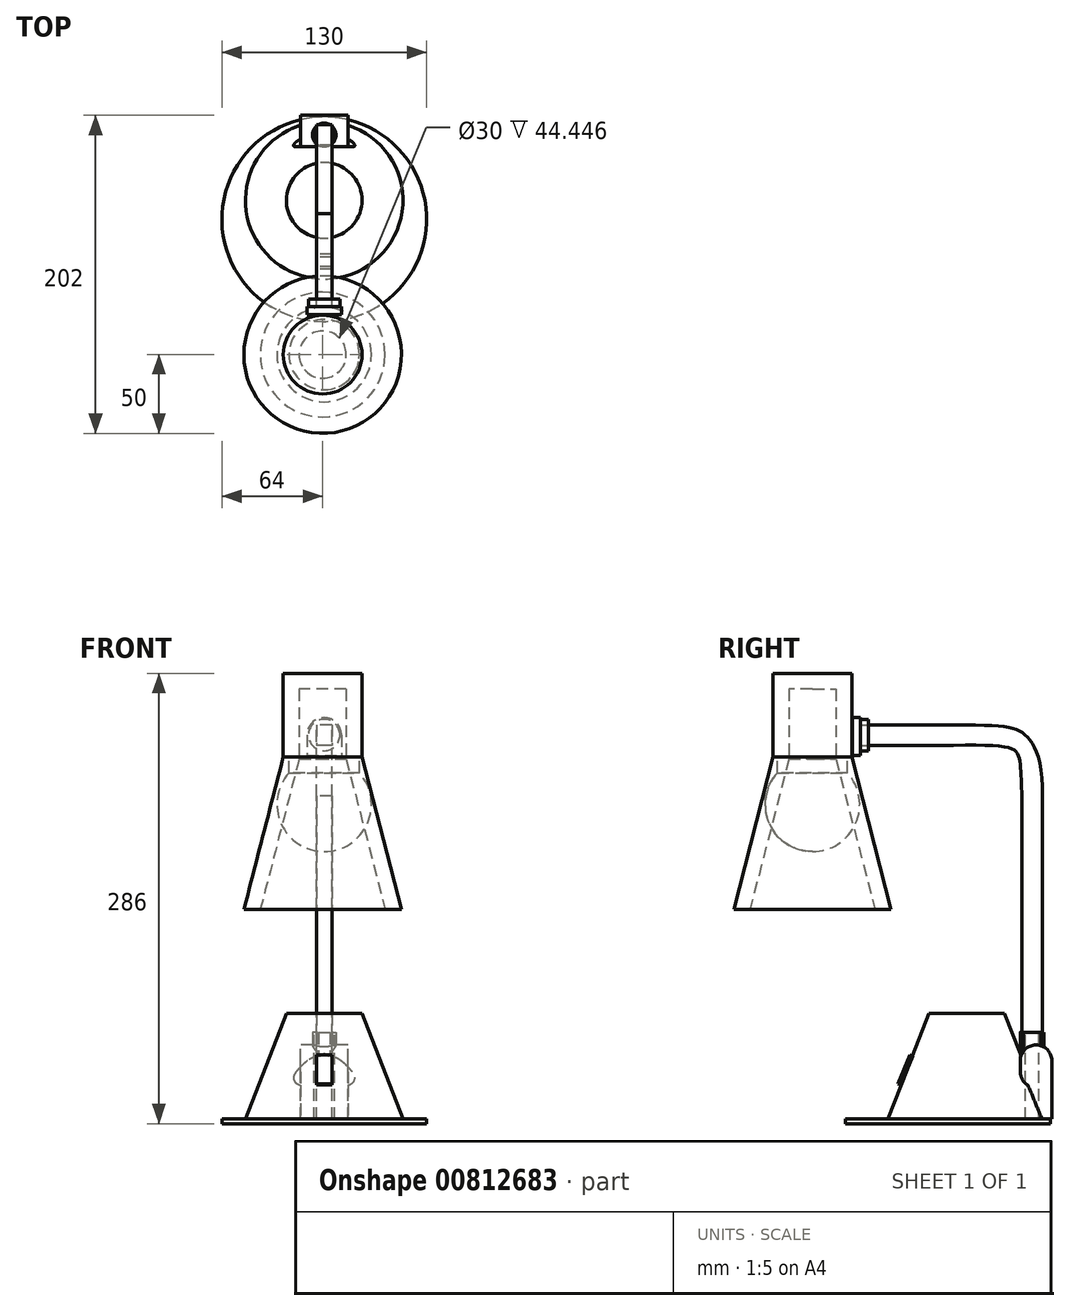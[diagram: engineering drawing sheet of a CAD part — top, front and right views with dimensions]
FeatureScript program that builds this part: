
annotation { "Feature Type Name" : "Feature", "Feature Type Description" : "" }
export const myFeature = defineFeature(function(context is Context, id is Id, definition is map)
    precondition{}
    {
        {
            var Q0;
            Q0=qCreatedBy(makeId("Top.planeOp"),FACE);
            var sketch = newSketch(context, id + "F0", { "sketchPlane" : qUnion([Q0])});
            skPoint(sketch, "E0.middle", {"position": v(0, 0) * mm});
            skCircle(sketch, "E1", {"center": v(0, 0) * mm, "radius": 65 * mm});
            skSolve(sketch);
        }
        {
            var Q0;
            Q0 = qSketchRegion(id + "F0", true);
            extrude(context, id + "F1", {"entities" : qUnion([Q0]), "depth" : 3 * mm, "offsetDistance" : 25 * mm});
        }
        {
            var Q0;
            Q0=makeQuery(id+"F1.opExtrude","CAP_FACE",FACE,{"disambiguationData":[OSD([sQuery(id+"F0.wireOp",EDGE,"E1")])],"isStart":false});
            var sketch = newSketch(context, id + "F2", { "sketchPlane" : qUnion([Q0])});
            skCircle(sketch, "E2", {"center": v(0, 12) * mm, "radius": 50 * mm});
            skSolve(sketch);
        }
        {
            var Q0;
            Q0=qCreatedBy(makeId("Top.planeOp"),FACE);
            cPlane(context, id + "F3", {"entities" : qUnion([Q0]), "cplaneType" : CPlaneType.OFFSET, "offset" : 70 * mm, "width" : 150 * mm, "height" : 150 * mm});
        }
        {
            var Q0;
            Q0=qCreatedBy(id+"F3.planeOp",FACE);
            var sketch = newSketch(context, id + "F4", { "sketchPlane" : qUnion([Q0])});
            skCircle(sketch, "E3", {"center": v(0, 12) * mm, "radius": 24 * mm});
            skSolve(sketch);
        }
        {
            var Q1;
            Q1=makeQuery(id+"F2.imprint","IMPRINT",FACE,{"disambiguationData":[TD([[makeQuery(id+"F2.imprint","IMPRINT",EDGE,{"derivedFrom":sQuery(id+"F2.wireOp",EDGE,"E2")}),1.0]])]});
            var Q2;
            Q2=makeQuery(id+"F4.imprint","IMPRINT",FACE,{"disambiguationData":[TD([[makeQuery(id+"F4.imprint","IMPRINT",EDGE,{"derivedFrom":sQuery(id+"F4.wireOp",EDGE,"E3")}),1.0]])]});
            loft(context, id + "F5", {"operationType" : NewBodyOperationType.ADD, "sheetProfilesArray" : [{ "sheetProfileEntities" : qUnion([Q1]) }, { "sheetProfileEntities" : qUnion([Q2]) }]});
        }
        {
            var Q0;
            Q0=qCreatedBy(makeId("Right.planeOp"),FACE);
            var sketch = newSketch(context, id + "F6", { "sketchPlane" : qUnion([Q0])});
            skLineSegment(sketch, "E4.bottom", {"start": v(46, 40) * mm, "end": v(56, 40) * mm});
            skLineSegment(sketch, "E4.top", {"start": v(46, 23) * mm, "end": v(56, 23) * mm});
            skLineSegment(sketch, "E4.left", {"start": v(46, 40) * mm, "end": v(46, 23) * mm});
            skLineSegment(sketch, "E4.right", {"start": v(56, 40) * mm, "end": v(56, 23) * mm});
            skSolve(sketch);
        }
        {
            var Q0;
            Q0=makeQuery(id+"F6.imprint","IMPRINT",FACE,{"disambiguationData":[TD([[makeQuery(id+"F6.imprint","IMPRINT",EDGE,{"derivedFrom":sQuery(id+"F6.wireOp",EDGE,"E4.bottom")}),-1.0]])]});
            extrude(context, id + "F7", {"entities" : qUnion([Q0]), "operationType" : NewBodyOperationType.REMOVE, "endBound" : BoundingType.SYMMETRIC, "depth" : 60 * mm, "offsetDistance" : 25 * mm});
        }
        {
            var Q0;
            Q0=makeQuery(id+"F7.boolean.opBoolean","COPY",EDGE,{"derivedFrom":makeQuery(id+"F7.opExtrude","SWEPT_EDGE",EDGE,{"disambiguationData":[OSD([sQuery(id+"F6.wireOp",EDGE,"E4.top"),sQuery(id+"F6.wireOp",EDGE,"E4.left")])]})});
            fillet(context, id + "F8", {"entities" : qUnion([Q0]), "radius" : 10 * mm, "tangentPropagation" : true, "allowEdgeOverflow" : false});
        }
        {
            var Q0;
            Q0=qCreatedBy(makeId("Right.planeOp"),FACE);
            var sketch = newSketch(context, id + "F9", { "sketchPlane" : qUnion([Q0])});
            skLineSegment(sketch, "E5", {"start": v(46, 3) * mm, "end": v(46, 40) * mm});
            skLineSegment(sketch, "E6", {"start": v(66, 3) * mm, "end": v(66, 40) * mm});
            skArc(sketch, "E7", {"start": v(56, 50) * mm, "mid": v(63.07, 47.07) * mm, "end": v(66, 40) * mm});
            skArc(sketch, "E8", {"start": v(46, 40) * mm, "mid": v(48.93, 47.07) * mm, "end": v(56, 50) * mm});
            skPoint(sketch, "E9", {"position": v(46, 53) * mm});
            skPoint(sketch, "E10", {"position": v(66, 53) * mm});
            skLineSegment(sketch, "E11", {"start": v(46, 3) * mm, "end": v(66, 3) * mm});
            skSolve(sketch);
        }
        {
            var Q0;
            Q0 = qSketchRegion(id + "F9", true);
            extrude(context, id + "F10", {"entities" : qUnion([Q0]), "operationType" : NewBodyOperationType.ADD, "endBound" : BoundingType.SYMMETRIC, "depth" : 30 * mm, "offsetDistance" : 25 * mm});
        }
        {
            var Q0;
            Q0=makeQuery(id+"F1.opExtrude","CAP_FACE",FACE,{"disambiguationData":[OSD([sQuery(id+"F0.wireOp",EDGE,"E1")])],"isStart":false});
            var sketch = newSketch(context, id + "F11", { "sketchPlane" : qUnion([Q0])});
            skCircle(sketch, "E12", {"center": v(0, 53.5) * mm, "radius": 7.5 * mm});
            skSolve(sketch);
        }
        {
            var Q0;
            Q0 = qSketchRegion(id + "F11", true);
            extrude(context, id + "F12", {"entities" : qUnion([Q0]), "operationType" : NewBodyOperationType.ADD, "depth" : 55 * mm, "offsetDistance" : 25 * mm});
        }
        {
            var Q0;
            Q0=makeQuery(id+"F12.opExtrude","CAP_FACE",FACE,{"disambiguationData":[OSD([sQuery(id+"F11.wireOp",EDGE,"E12")])],"isStart":false});
            var sketch = newSketch(context, id + "F13", { "sketchPlane" : qUnion([Q0])});
            skCircle(sketch, "E13.0", {"center": v(0, 53.5) * mm, "radius": 6.5 * mm});
            skSolve(sketch);
        }
        {
            var Q0;
            Q0 = qSketchRegion(id + "F13", true);
            var Q1;
            Q1=makeQuery(id+"F1.opExtrude","CAP_FACE",FACE,{"disambiguationData":[OSD([sQuery(id+"F0.wireOp",EDGE,"E1")])],"isStart":false});
            extrude(context, id + "F14", {"entities" : qUnion([Q0]), "operationType" : NewBodyOperationType.REMOVE, "endBound" : BoundingType.UP_TO_SURFACE, "oppositeDirection" : true, "depth" : 25 * mm, "endBoundEntityFace" : qUnion([Q1]), "offsetDistance" : 25 * mm});
        }
        {
            var Q0;
            Q0=makeQuery(id+"F5.opLoft","CAP_FACE",FACE,{"disambiguationData":[OSD([makeQuery(id+"F4.imprint","IMPRINT",FACE,{"disambiguationData":[TD([[makeQuery(id+"F4.imprint","IMPRINT",EDGE,{"derivedFrom":sQuery(id+"F4.wireOp",EDGE,"E3")}),1.0]])]})])],"isStart":true});
            cPlane(context, id + "F15", {"entities" : qUnion([Q0]), "cplaneType" : CPlaneType.OFFSET, "offset" : 5 * mm, "oppositeDirection" : true, "width" : 150 * mm, "height" : 150 * mm});
        }
        {
            var Q0;
            Q0=qCreatedBy(makeId("Right.planeOp"),FACE);
            cPlane(context, id + "F16", {"entities" : qUnion([Q0]), "cplaneType" : CPlaneType.OFFSET, "offset" : 5 * mm, "oppositeDirection" : true, "width" : 150 * mm, "height" : 150 * mm});
        }
        {
            var Q0;
            Q0=qCreatedBy(id+"F16.planeOp",FACE);
            var sketch = newSketch(context, id + "F17", { "sketchPlane" : qUnion([Q0])});
            skLineSegment(sketch, "E14.0", {"start": v(46, 58) * mm, "end": v(61, 58) * mm});
            skLineSegment(sketch, "E15.0", {"start": v(47, 58) * mm, "end": v(60, 58) * mm});
            skSolve(sketch);
        }
        {
            var Q0;
            Q0=qCreatedBy(id+"F16.planeOp",FACE);
            var sketch = newSketch(context, id + "F18", { "sketchPlane" : qUnion([Q0])});
            skLineSegment(sketch, "E16.bottom", {"start": v(60, 3) * mm, "end": v(47, 3) * mm});
            skLineSegment(sketch, "E17", {"start": v(47, 58) * mm, "end": v(47, 208) * mm});
            skLineSegment(sketch, "E18", {"start": v(60, 58) * mm, "end": v(60, 208) * mm});
            skFitSpline(sketch, "E19", {"points": [v(60, 208) * mm, v(48.55, 247.3) * mm, v(3.39, 253.37) * mm], "startDerivative": vector(2.49, 149.87) * mm, "endDerivative": vector(-184.82, 1.92) * mm});
            skFitSpline(sketch, "E20", {"points": [v(47, 208) * mm, v(45.35, 231.77) * mm, v(3.39, 240.37) * mm], "startDerivative": vector(-2.36, 61.21) * mm, "endDerivative": vector(-191.9, -1.87) * mm});
            skLineSegment(sketch, "E21", {"start": v(3.39, 253.37) * mm, "end": v(-50.61, 253.37) * mm});
            skLineSegment(sketch, "E22", {"start": v(3.39, 240.37) * mm, "end": v(-50.61, 240.37) * mm});
            skLineSegment(sketch, "E23", {"start": v(-50.61, 253.37) * mm, "end": v(-50.61, 240.37) * mm});
            skLineSegment(sketch, "E24", {"start": v(60, 58) * mm, "end": v(60, 3) * mm});
            skLineSegment(sketch, "E25", {"start": v(47, 58) * mm, "end": v(47, 3) * mm});
            skSolve(sketch);
        }
        {
            var Q0;
            Q0=makeQuery(id+"F18.imprint","IMPRINT",FACE,{"disambiguationData":[TD([[makeQuery(id+"F18.imprint","IMPRINT",EDGE,{"derivedFrom":sQuery(id+"F18.wireOp",EDGE,"E16.bottom")}),-1.0]])]});
            extrude(context, id + "F19", {"entities" : qUnion([Q0]), "operationType" : NewBodyOperationType.ADD, "depth" : 10 * mm, "offsetDistance" : 25 * mm});
        }
        {
            var Q0;
            Q0=makeQuery(id+"F19.opExtrude","SWEPT_FACE",FACE,{"disambiguationData":[OSD([sQuery(id+"F18.wireOp",EDGE,"E23")])]});
            var sketch = newSketch(context, id + "F20", { "sketchPlane" : qUnion([Q0])});
            skCircle(sketch, "E26", {"center": v(0, 246.87) * mm, "radius": 10 * mm});
            skPoint(sketch, "E26.centerSnap0", {"position": v(5, 246.87) * mm});
            skSolve(sketch);
        }
        {
            var Q0;
            Q0=makeQuery(id+"F20.imprint","IMPRINT",FACE,{"disambiguationData":[TD([[makeQuery(id+"F20.imprint","IMPRINT",EDGE,{"derivedFrom":sQuery(id+"F20.wireOp",EDGE,"E26")}),1.0]])]});
            extrude(context, id + "F21", {"entities" : qUnion([Q0]), "operationType" : NewBodyOperationType.ADD, "depth" : 5 * mm, "offsetDistance" : 25 * mm});
        }
        {
            var Q0;
            Q0=makeQuery(id+"F21.opExtrude","CAP_FACE",FACE,{"disambiguationData":[OSD([sQuery(id+"F18.wireOp",EDGE,"E21"),sQuery(id+"F18.wireOp",EDGE,"E22"),sQuery(id+"F18.wireOp",EDGE,"E23"),sQuery(id+"F20.wireOp",EDGE,"E26")])],"isStart":false});
            var sketch = newSketch(context, id + "F22", { "sketchPlane" : qUnion([Q0])});
            skArc(sketch, "E27", {"start": v(0, 257.87) * mm, "mid": v(7.78, 254.65) * mm, "end": v(11, 246.87) * mm});
            skArc(sketch, "E28", {"start": v(0, 257.87) * mm, "mid": v(-7.78, 254.65) * mm, "end": v(-11, 246.87) * mm});
            skLineSegment(sketch, "E29.bottom", {"start": v(-11, 246.87) * mm, "end": v(11, 246.87) * mm});
            skLineSegment(sketch, "E29.top", {"start": v(-11, 234) * mm, "end": v(11, 234) * mm});
            skLineSegment(sketch, "E29.left", {"start": v(-11, 246.87) * mm, "end": v(-11, 234) * mm});
            skLineSegment(sketch, "E29.right", {"start": v(11, 246.87) * mm, "end": v(11, 234) * mm});
            skSolve(sketch);
        }
        {
            var Q0;
            Q0 = qSketchRegion(id + "F22", true);
            extrude(context, id + "F23", {"entities" : qUnion([Q0]), "operationType" : NewBodyOperationType.ADD, "depth" : 5 * mm, "offsetDistance" : 25 * mm});
        }
        {
            var Q0;
            Q0=qCreatedBy(makeId("Right.planeOp"),FACE);
            var sketch = newSketch(context, id + "F24", { "sketchPlane" : qUnion([Q0])});
            skLineSegment(sketch, "E30", {"start": v(0, 0) * mm, "end": v(0, 150) * mm});
            skLineSegment(sketch, "E31", {"start": v(0, 0) * mm, "end": v(-50, 0) * mm});
            skLineSegment(sketch, "E32", {"start": v(-50, 0) * mm, "end": v(-25, 96.82) * mm});
            skLineSegment(sketch, "E33", {"start": v(-25, 96.82) * mm, "end": v(-25, 150) * mm});
            skLineSegment(sketch, "E34", {"start": v(-25, 150) * mm, "end": v(0, 150) * mm});
            skSolve(sketch);
        }
        {
            var Q0;
            Q0=makeQuery(id+"F24.imprint","IMPRINT",FACE,{"disambiguationData":[TD([[makeQuery(id+"F24.imprint","IMPRINT",EDGE,{"derivedFrom":sQuery(id+"F24.wireOp",EDGE,"E30")}),1.0]])]});
            var Q1;
            Q1=sQuery(id+"F24.wireOp",EDGE,"E30");
            revolve(context, id + "F25", {"surfaceOperationType" : NewSurfaceOperationType.NEW, "entities" : qUnion([Q0]), "axis" : qUnion([Q1]), "revolveType" : RevolveType.FULL});
        }
        {
            var Q0;
            Q0=makeQuery(id+"F25.opRevolve","SWEPT_FACE",FACE,{"disambiguationData":[OSD([sQuery(id+"F24.wireOp",EDGE,"E31")])]});
            shell(context, id + "F26", {"entities" : qUnion([Q0]), "thickness" : 10 * mm});
        }
        {
            var Q0;
            Q0=makeQuery(id+"F25.opRevolve","SWEPT_BODY",BODY,{"disambiguationData":[OSD([sQuery(id+"F24.wireOp",EDGE,"E30"),sQuery(id+"F24.wireOp",EDGE,"E31"),sQuery(id+"F24.wireOp",EDGE,"E32"),sQuery(id+"F24.wireOp",EDGE,"E33"),sQuery(id+"F24.wireOp",EDGE,"E34")])]});
            transform(context, id + "F27", {"entities" : qUnion([Q0]), "transformType" : TransformType.TRANSLATION_3D, "dx" : -1 * mm, "dy" : -86 * mm, "dz" : 136 * mm, "makeCopy" : false});
        }
        {
            var Q0;
            Q0=makeQuery(id+"F25.opRevolve","SWEPT_FACE",FACE,{"disambiguationData":[OSD([sQuery(id+"F24.wireOp",EDGE,"E34")])]});
            var sketch = newSketch(context, id + "F28", { "sketchPlane" : qUnion([Q0])});
            skLineSegment(sketch, "E35", {"start": v(0, -61.02) * mm, "end": v(0, -110.98) * mm, "construction": true});
            skPoint(sketch, "E36", {"position": v(0, -86) * mm});
            skSolve(sketch);
        }
        {
            var Q0;
            Q0=qCreatedBy(makeId("Right.planeOp"),FACE);
            var sketch = newSketch(context, id + "F29", { "sketchPlane" : qUnion([Q0])});
            skLineSegment(sketch, "E37", {"start": v(-86, 232.82) * mm, "end": v(-86, 172.82) * mm});
            skLineSegment(sketch, "E38", {"start": v(-86, 232.82) * mm, "end": v(-63.64, 232.82) * mm});
            skLineSegment(sketch, "E39", {"start": v(-63.64, 232.82) * mm, "end": v(-63.64, 222.82) * mm});
            skArc(sketch, "E40", {"start": v(-86, 172.82) * mm, "mid": v(-58.61, 190.58) * mm, "end": v(-63.64, 222.82) * mm});
            skSolve(sketch);
        }
        {
            var Q0;
            Q0 = qSketchRegion(id + "F29", true);
            var Q1;
            Q1=sQuery(id+"F29.wireOp",EDGE,"E37");
            revolve(context, id + "F30", {"surfaceOperationType" : NewSurfaceOperationType.NEW, "entities" : qUnion([Q0]), "axis" : qUnion([Q1]), "revolveType" : RevolveType.FULL});
        }
        {
            var Q0;
            Q0=qCreatedBy(makeId("Front.planeOp"),FACE);
            cPlane(context, id + "F31", {"entities" : qUnion([Q0]), "cplaneType" : CPlaneType.OFFSET, "offset" : 25 * mm, "width" : 150 * mm, "height" : 150 * mm});
        }
        {
            var Q0;
            Q0=qCreatedBy(id+"F31.planeOp",FACE);
            var sketch = newSketch(context, id + "F32", { "sketchPlane" : qUnion([Q0])});
            skLineSegment(sketch, "E41.bottom", {"start": v(5, 23) * mm, "end": v(-5, 23) * mm});
            skLineSegment(sketch, "E41.top", {"start": v(5, 43) * mm, "end": v(-5, 43) * mm});
            skLineSegment(sketch, "E41.left", {"start": v(5, 23) * mm, "end": v(5, 43) * mm});
            skLineSegment(sketch, "E41.right", {"start": v(-5, 23) * mm, "end": v(-5, 43) * mm});
            skPoint(sketch, "E41.middle", {"position": v(0, 33) * mm});
            skSolve(sketch);
        }
        {
            var Q0;
            Q0=makeQuery(id+"F32.imprint","IMPRINT",FACE,{"disambiguationData":[TD([[makeQuery(id+"F32.imprint","IMPRINT",EDGE,{"derivedFrom":sQuery(id+"F32.wireOp",EDGE,"E41.bottom")}),-1.0]])]});
            extrude(context, id + "F33", {"entities" : qUnion([Q0]), "depth" : 2 * mm, "offsetDistance" : 25 * mm});
        }
        {
            var Q0;
            Q0=makeQuery(id+"F33.opExtrude","SWEPT_BODY",BODY,{"disambiguationData":[OSD([sQuery(id+"F32.wireOp",EDGE,"E41.bottom"),sQuery(id+"F32.wireOp",EDGE,"E41.top"),sQuery(id+"F32.wireOp",EDGE,"E41.left"),sQuery(id+"F32.wireOp",EDGE,"E41.right")])]});
            var Q1;
            Q1=makeQuery(id+"F33.opExtrude","CAP_EDGE",EDGE,{"disambiguationData":[OSD([sQuery(id+"F32.wireOp",EDGE,"E41.top")])],"isStart":true});
            transform(context, id + "F34", {"entities" : qUnion([Q0]), "transformType" : TransformType.ROTATION, "transformAxis" : qUnion([Q1]), "angle" : 22.82 * degree, "makeCopy" : false});
        }
        {
            var Q0;
            Q0=makeQuery(id+"F33.opExtrude","SWEPT_BODY",BODY,{"disambiguationData":[OSD([sQuery(id+"F32.wireOp",EDGE,"E41.bottom"),sQuery(id+"F32.wireOp",EDGE,"E41.top"),sQuery(id+"F32.wireOp",EDGE,"E41.left"),sQuery(id+"F32.wireOp",EDGE,"E41.right")])]});
            transform(context, id + "F35", {"entities" : qUnion([Q0]), "transformType" : TransformType.TRANSLATION_3D, "dx" : 0 * mm, "dy" : 2.8 * mm, "dz" : 0 * mm, "makeCopy" : false});
        }
    });
